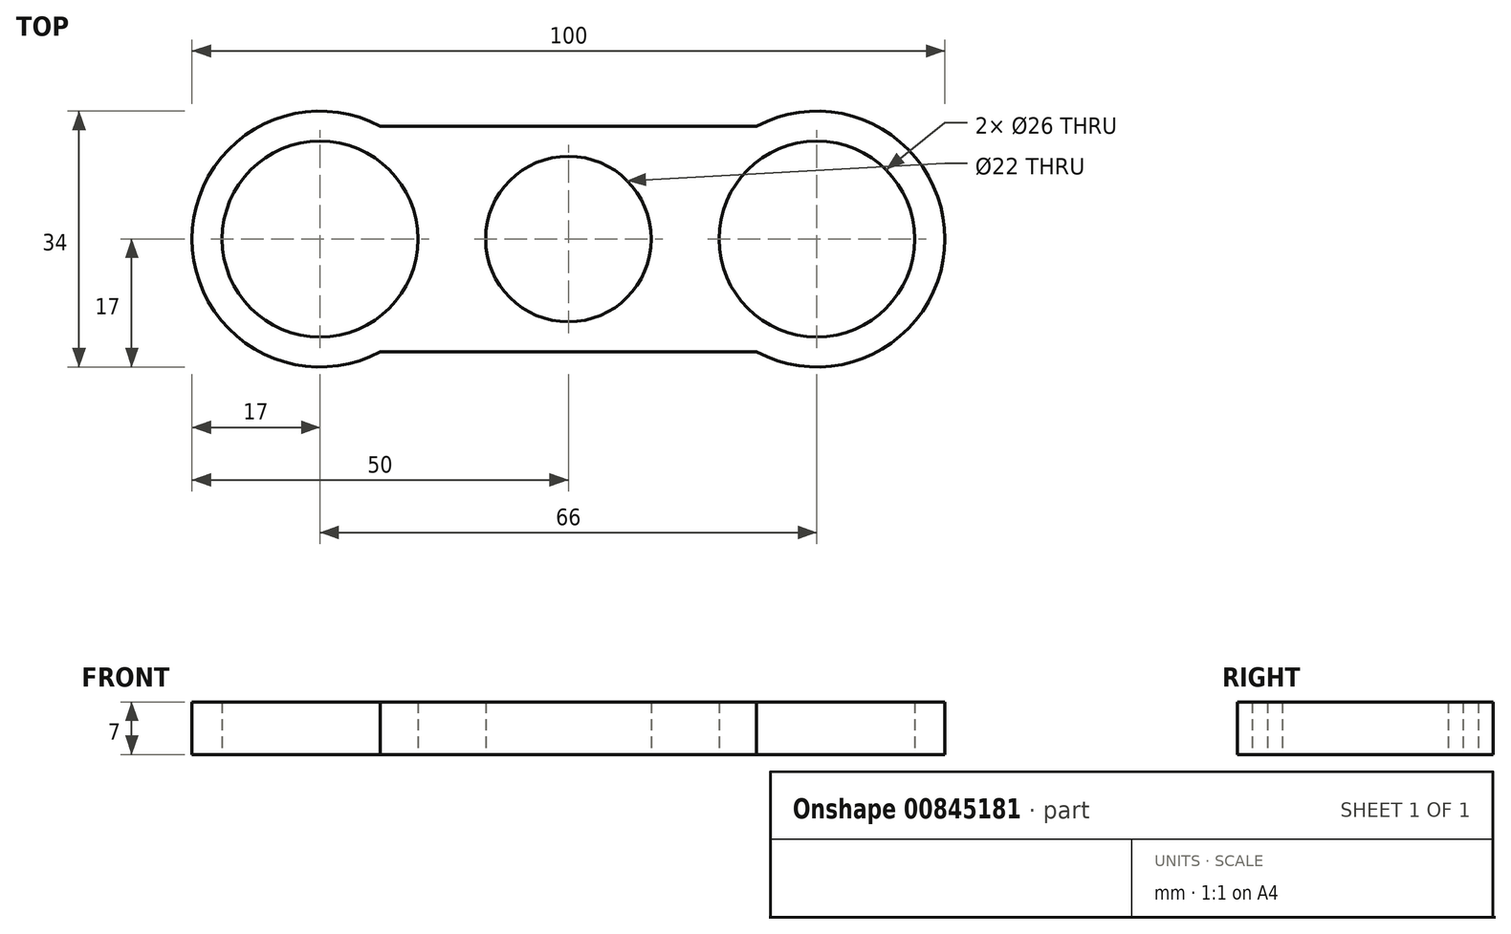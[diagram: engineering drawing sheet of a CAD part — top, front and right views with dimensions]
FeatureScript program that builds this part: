
annotation { "Feature Type Name" : "Feature", "Feature Type Description" : "" }
export const myFeature = defineFeature(function(context is Context, id is Id, definition is map)
    precondition{}
    {
        {
            var Q0;
            Q0=qCreatedBy(makeId("Top.planeOp"),FACE);
            var sketch = newSketch(context, id + "F0", { "sketchPlane" : qUnion([Q0])});
            skArc(sketch, "E0.1.3", {"start": v(-25, 15) * mm, "mid": v(-50, 0) * mm, "end": v(-25, -15) * mm});
            skPoint(sketch, "E0.center", {"position": v(0, 0) * mm});
            skLineSegment(sketch, "E1", {"start": v(-25, -15) * mm, "end": v(0, -15) * mm});
            skCircle(sketch, "E2", {"center": v(-33, 0) * mm, "radius": 13 * mm});
            skLineSegment(sketch, "E3.MirrorCS", {"start": v(25, -15) * mm, "end": v(0, -15) * mm});
            skArc(sketch, "E4.MirrorCS", {"start": v(25, 15) * mm, "mid": v(50, 0) * mm, "end": v(25, -15) * mm});
            skCircle(sketch, "E5.MirrorC", {"center": v(33, 0) * mm, "radius": 13 * mm});
            skPoint(sketch, "E6.orphan", {"position": v(0, 41.08) * mm});
            skCircle(sketch, "E7", {"center": v(0, 0) * mm, "radius": 11 * mm});
            skLineSegment(sketch, "E8", {"start": v(-25, 15) * mm, "end": v(25, 15) * mm});
            skSolve(sketch);
        }
        {
            var Q0;
            Q0=qSketchRegion(id+"F0",true);
            extrude(context, id + "F1", {"entities" : qUnion([Q0]), "depth" : 7 * mm, "offsetDistance" : 25 * mm});
        }
    });
